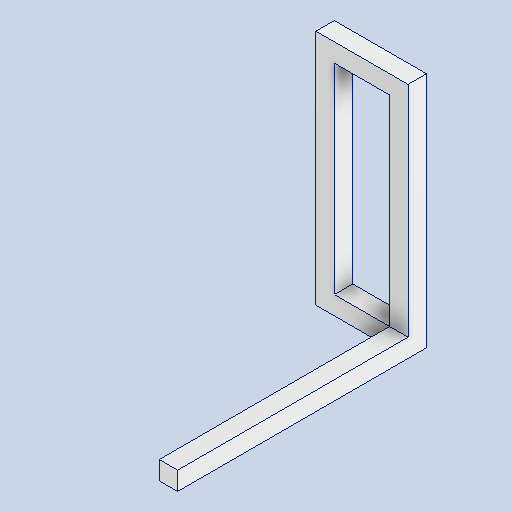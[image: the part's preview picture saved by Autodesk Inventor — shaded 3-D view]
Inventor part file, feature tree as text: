
AUTODESK INVENTOR PART (.ipt)
format: ipt  version: 2025 (Build 290162010, 162A)  size: 119,808 bytes
history: native  units: mm
features: other x3, sketch x2
ambient origin geometry x8: Origin, YZ Plane, XZ Plane, XY Plane, X Axis, Y Axis, Z Axis, Center Point
bodies: Volumenkörper1 (feature_tree)
feature tree (5):
  other  "FrameSide.ipt"
  other  "Volumenkörper1::FrameSide.ipt"
  other  "Bezeichnung1"
  sketch  "Skizze1"  dims[d0=10.0mm]
  sketch  "Skizze2"
